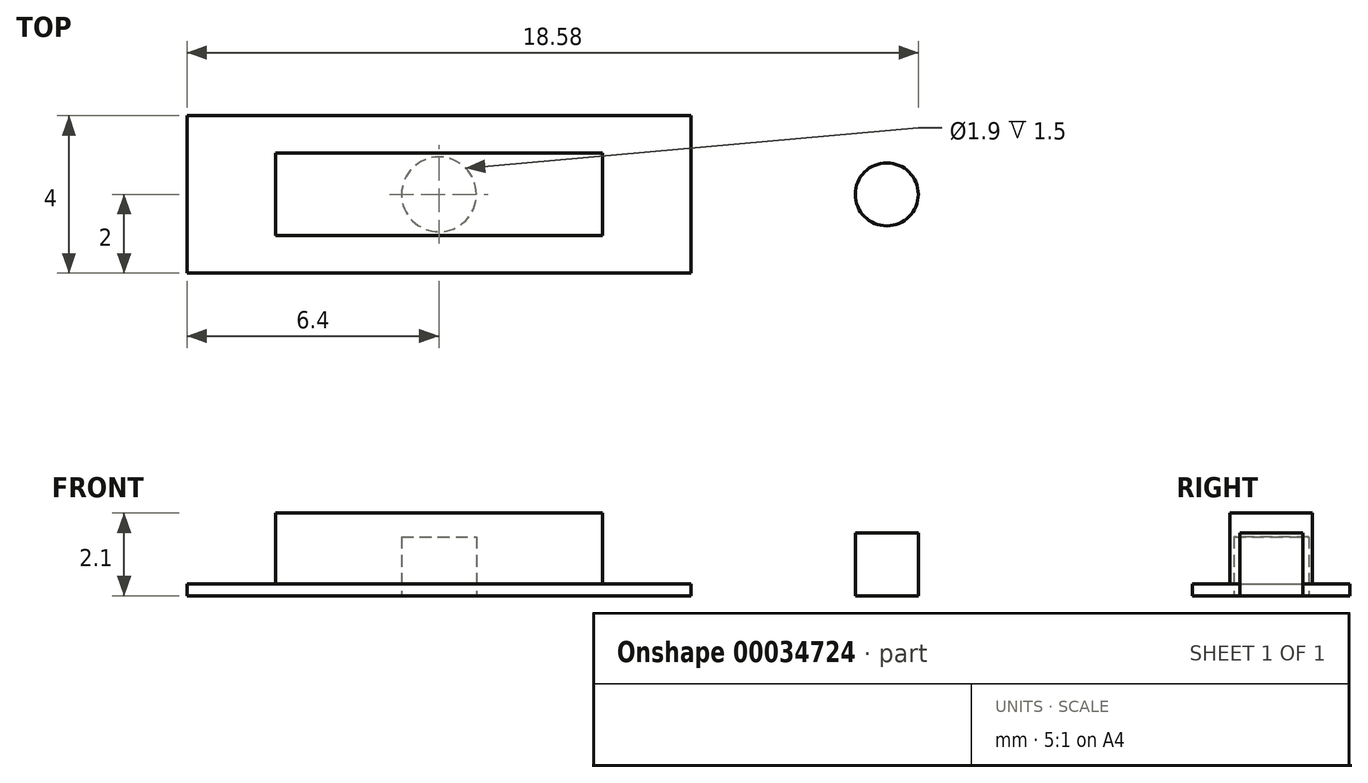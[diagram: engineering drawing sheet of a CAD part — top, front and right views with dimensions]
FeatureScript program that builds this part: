
annotation { "Feature Type Name" : "Feature", "Feature Type Description" : "" }
export const myFeature = defineFeature(function(context is Context, id is Id, definition is map)
    precondition{}
    {
        {
            var Q0;
            Q0=qCreatedBy(makeId("Top.planeOp"),FACE);
            var sketch = newSketch(context, id + "F0", { "sketchPlane" : qUnion([Q0])});
            skLineSegment(sketch, "E0.bottom", {"start": v(6.4, -2) * mm, "end": v(-6.4, -2) * mm});
            skLineSegment(sketch, "E0.top", {"start": v(6.4, 2) * mm, "end": v(-6.4, 2) * mm});
            skLineSegment(sketch, "E0.left", {"start": v(6.4, -2) * mm, "end": v(6.4, 2) * mm});
            skLineSegment(sketch, "E0.right", {"start": v(-6.4, -2) * mm, "end": v(-6.4, 2) * mm});
            skPoint(sketch, "E0.middle", {"position": v(0, 0) * mm});
            skLineSegment(sketch, "E1.bottom", {"start": v(4.15, 1.05) * mm, "end": v(-4.15, 1.05) * mm});
            skLineSegment(sketch, "E1.top", {"start": v(4.15, -1.05) * mm, "end": v(-4.15, -1.05) * mm});
            skLineSegment(sketch, "E1.left", {"start": v(4.15, 1.05) * mm, "end": v(4.15, -1.05) * mm});
            skLineSegment(sketch, "E1.right", {"start": v(-4.15, 1.05) * mm, "end": v(-4.15, -1.05) * mm});
            skSolve(sketch);
        }
        {
            var Q0;
            Q0=makeQuery(id+"F0.imprint","IMPRINT",FACE,{"disambiguationData":[TD([[makeQuery(id+"F0.imprint","IMPRINT",EDGE,{"derivedFrom":sQuery(id+"F0.wireOp",EDGE,"E0.bottom")}),-1.0]])]});
            var Q1;
            Q1=makeQuery(id+"F0.imprint","IMPRINT",FACE,{"disambiguationData":[TD([[makeQuery(id+"F0.imprint","IMPRINT",EDGE,{"derivedFrom":sQuery(id+"F0.wireOp",EDGE,"E1.bottom")}),1.0]])]});
            extrude(context, id + "F1", {"entities" : qUnion([Q0, Q1]), "depth" : 0.3 * mm});
        }
        {
            var Q0;
            Q0=makeQuery(id+"F0.imprint","IMPRINT",FACE,{"disambiguationData":[TD([[makeQuery(id+"F0.imprint","IMPRINT",EDGE,{"derivedFrom":sQuery(id+"F0.wireOp",EDGE,"E1.bottom")}),1.0]])]});
            extrude(context, id + "F2", {"entities" : qUnion([Q0]), "operationType" : NewBodyOperationType.ADD, "depth" : 2.1 * mm});
        }
        {
            var Q0;
            Q0=makeQuery(id+"F1.opExtrude","CAP_FACE",FACE,{"disambiguationData":[OSD([sQuery(id+"F0.wireOp",EDGE,"E0.bottom"),sQuery(id+"F0.wireOp",EDGE,"E0.top"),sQuery(id+"F0.wireOp",EDGE,"E0.left"),sQuery(id+"F0.wireOp",EDGE,"E0.right")])],"isStart":true});
            var sketch = newSketch(context, id + "F3", { "sketchPlane" : qUnion([Q0])});
            skCircle(sketch, "E2", {"center": v(0, 0) * mm, "radius": 0.95 * mm});
            skSolve(sketch);
        }
        {
            var Q0;
            Q0=makeQuery(id+"F3.imprint","IMPRINT",FACE,{"disambiguationData":[TD([[makeQuery(id+"F3.imprint","IMPRINT",EDGE,{"derivedFrom":sQuery(id+"F3.wireOp",EDGE,"E2")}),1.0]])]});
            extrude(context, id + "F4", {"entities" : qUnion([Q0]), "operationType" : NewBodyOperationType.REMOVE, "oppositeDirection" : true, "depth" : 1.5 * mm});
        }
        {
            var Q0;
            Q0=qCreatedBy(makeId("Top.planeOp"),FACE);
            var sketch = newSketch(context, id + "F5", { "sketchPlane" : qUnion([Q0])});
            skCircle(sketch, "E3", {"center": v(11.38, 0) * mm, "radius": 0.8 * mm});
            skSolve(sketch);
        }
        {
            var Q0;
            Q0=makeQuery(id+"F5.imprint","IMPRINT",FACE,{"disambiguationData":[TD([[makeQuery(id+"F5.imprint","IMPRINT",EDGE,{"derivedFrom":sQuery(id+"F5.wireOp",EDGE,"E3")}),1.0]])]});
            extrude(context, id + "F6", {"entities" : qUnion([Q0]), "depth" : 1.6 * mm});
        }
    });
